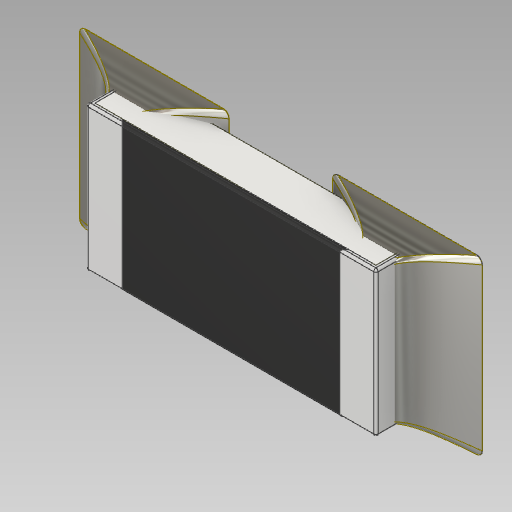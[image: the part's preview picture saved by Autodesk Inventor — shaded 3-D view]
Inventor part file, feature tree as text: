
AUTODESK INVENTOR PART (.ipt)
format: ipt  version: 2020 (Build 240168000, 168)  size: 444,928 bytes
history: native  units: in
note: dims shown in document units (in); Inventor stores cm internally (conversion verified against a paired STEP export)
features: other x4, plane x3, sketch x3, extrude x1, fillet x1, loft x1, mirror x1, projected_geometry x1
ambient origin geometry x8: Origin, YZ Plane, XZ Plane, XY Plane, X Axis, Y Axis, Z Axis, Center Point
bodies: Solid1 (feature_tree), Solid2 (feature_tree), Solid3 (feature_tree), Solid4 (feature_tree), Solid5 (feature_tree)
feature tree (15):
  extrude  "Extrusion1"  Depth=0.075in
  plane  "Work Plane1"
  fillet  "Fillet1"  Radius=0.065in
  loft  "Loft1"
  plane  "Work Plane2"
  mirror  "Mirror1"
  sketch  "Sketch1"  dims[d1=0.0875in d2=0.075in d3=0.065in]
  sketch  "Sketch2"  dims[d4=0.0001in d5=0.0in d6=-0.0025in]
  sketch  "Sketch3"  dims[d7=0.001in d8=0.0025in d9=0.4921in d10=90.0deg d11=0.0in d12=90.0deg d13=0.0013in]
  projected_geometry  "Projected Loop2"
  plane  "Work Plane3"
  other  "lead2"
  other  "lead1"
  other  "substrate"
  other  "overglaze"
